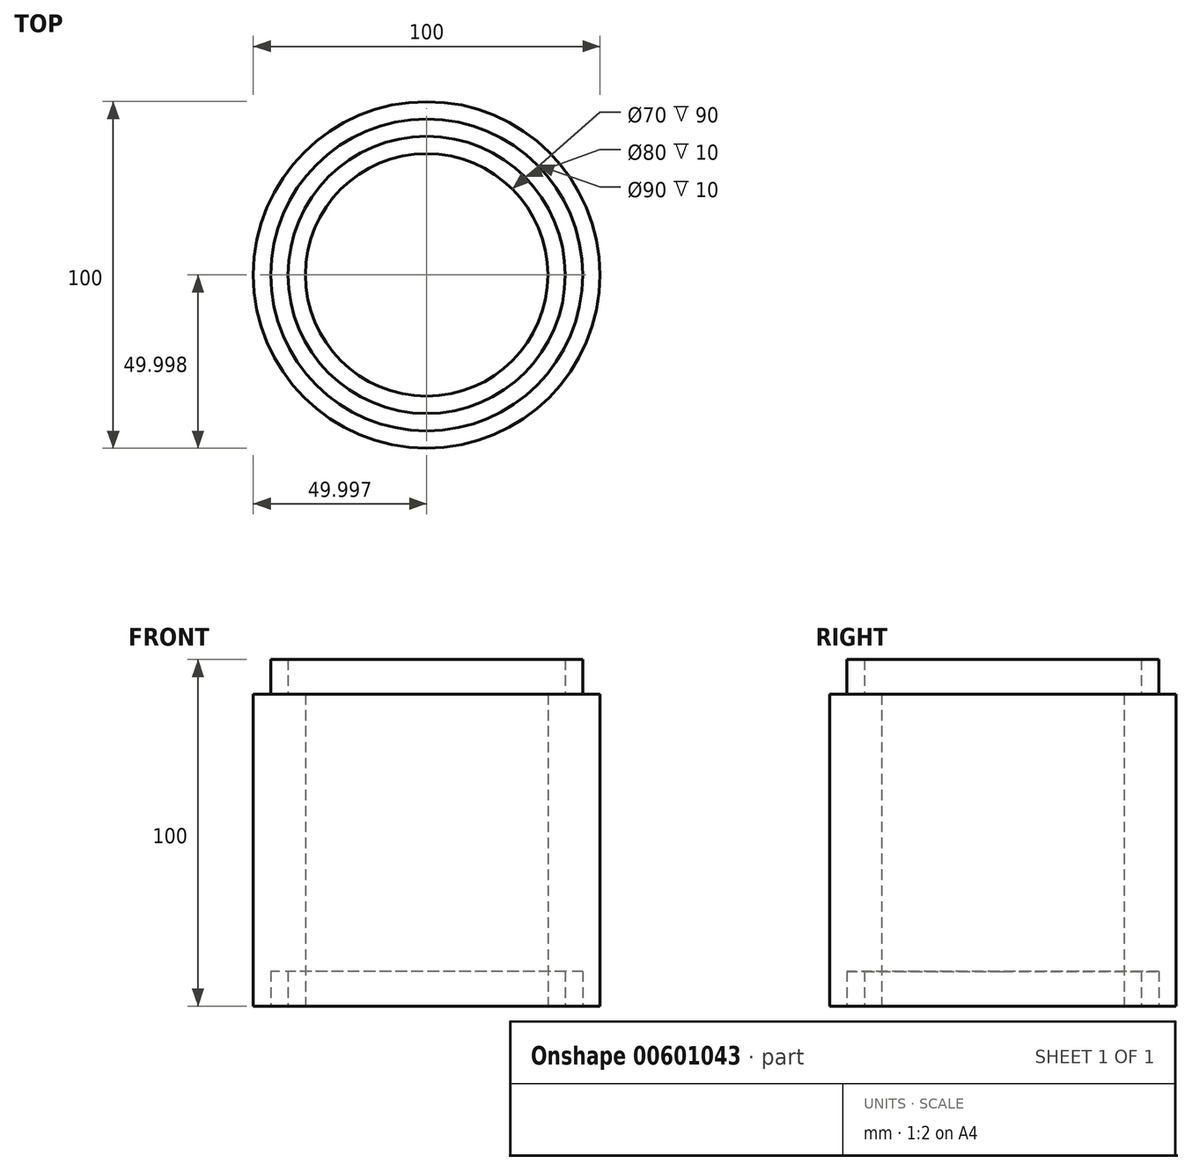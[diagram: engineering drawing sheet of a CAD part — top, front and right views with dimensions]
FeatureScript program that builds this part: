
annotation { "Feature Type Name" : "Feature", "Feature Type Description" : "" }
export const myFeature = defineFeature(function(context is Context, id is Id, definition is map)
    precondition{}
    {
        {
            var Q0;
            Q0=qCreatedBy(makeId("Top.planeOp"),FACE);
            var sketch = newSketch(context, id + "F0", { "sketchPlane" : qUnion([Q0])});
            skCircle(sketch, "E0", {"center": v(-87.7, -2.87) * mm, "radius": 50 * mm});
            skCircle(sketch, "E1", {"center": v(-87.7, -2.87) * mm, "radius": 45 * mm});
            skCircle(sketch, "E2", {"center": v(-87.7, -2.87) * mm, "radius": 40 * mm});
            skCircle(sketch, "E3", {"center": v(-87.7, -2.87) * mm, "radius": 35 * mm});
            skSolve(sketch);
        }
        {
            var Q0;
            Q0 = qSketchRegion(id + "F0", true);
            var Q1;
            Q1=makeQuery(id+"F0.imprint","IMPRINT",FACE,{"disambiguationData":[TD([[makeQuery(id+"F0.imprint","IMPRINT",EDGE,{"derivedFrom":sQuery(id+"F0.wireOp",EDGE,"E2")}),1.0]])]});
            var Q2;
            Q2=makeQuery(id+"F0.imprint","IMPRINT",FACE,{"disambiguationData":[TD([[makeQuery(id+"F0.imprint","IMPRINT",EDGE,{"derivedFrom":sQuery(id+"F0.wireOp",EDGE,"E1")}),1.0]])]});
            extrude(context, id + "F1", {"entities" : qUnion([Q0, Q1, Q2]), "depth" : 90 * mm, "offsetDistance" : 25 * mm});
        }
        {
            var Q0;
            Q0=makeQuery(id+"F0.imprint","IMPRINT",FACE,{"disambiguationData":[TD([[makeQuery(id+"F0.imprint","IMPRINT",EDGE,{"derivedFrom":sQuery(id+"F0.wireOp",EDGE,"E1")}),1.0]])]});
            extrude(context, id + "F2", {"entities" : qUnion([Q0]), "operationType" : NewBodyOperationType.ADD, "depth" : 100 * mm, "offsetDistance" : 25 * mm});
        }
        {
            var Q0;
            Q0=makeQuery(id+"F0.imprint","IMPRINT",FACE,{"disambiguationData":[TD([[makeQuery(id+"F0.imprint","IMPRINT",EDGE,{"derivedFrom":sQuery(id+"F0.wireOp",EDGE,"E1")}),1.0]])]});
            extrude(context, id + "F3", {"entities" : qUnion([Q0]), "operationType" : NewBodyOperationType.REMOVE, "depth" : 10 * mm, "offsetDistance" : 25 * mm});
        }
    });
